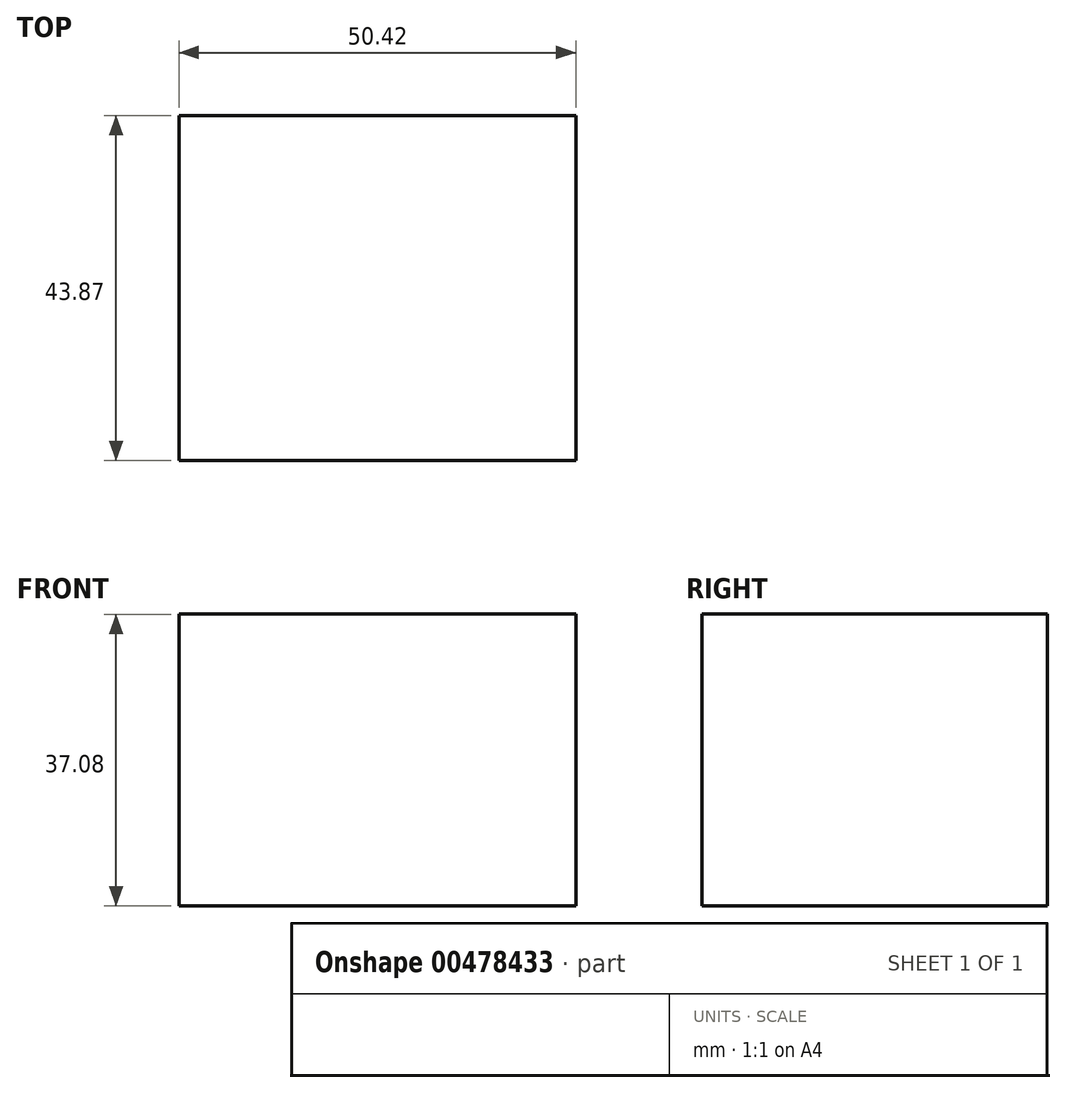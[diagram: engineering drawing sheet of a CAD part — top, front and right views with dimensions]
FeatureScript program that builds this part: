
annotation { "Feature Type Name" : "Feature", "Feature Type Description" : "" }
export const myFeature = defineFeature(function(context is Context, id is Id, definition is map)
    precondition{}
    {
        {
            var Q0;
            Q0=qCreatedBy(makeId("Top.planeOp"),FACE);
            var sketch = newSketch(context, id + "F0", { "sketchPlane" : qUnion([Q0])});
            skLineSegment(sketch, "E0", {"start": v(-37.71, -21.9) * mm, "end": v(12.7, -21.9) * mm});
            skLineSegment(sketch, "E1", {"start": v(12.7, -21.9) * mm, "end": v(12.7, 21.96) * mm});
            skLineSegment(sketch, "E2", {"start": v(12.7, 21.96) * mm, "end": v(-37.71, 21.96) * mm});
            skLineSegment(sketch, "E3", {"start": v(-37.71, 21.96) * mm, "end": v(-37.71, -21.9) * mm});
            skSolve(sketch);
        }
        {
            var Q0;
            Q0 = qSketchRegion(id + "F0", true);
            extrude(context, id + "F1", {"entities" : qUnion([Q0]), "depth" : 37.08 * mm});
        }
    });
